annotation { "Feature Type Name" : "Feature", "Feature Type Description" : "" }
export const myFeature = defineFeature(function(context is Context, id is Id, definition is map)
    precondition{}
    {
        {
            var Q0;
            Q0=qCreatedBy(makeId("Top.planeOp"),FACE);
            var sketch = newSketch(context, id + "F0", { "sketchPlane" : qUnion([Q0])});
            skText(sketch, "E0", { "text": "DROID SANS MONO", "fontName": "DroidSansMono.ttf"});
            skText(sketch, "E1", { "text": "ALLERTA STENCIL", "fontName": "AllertaStencil-Regular.ttf"});
            skText(sketch, "E2", { "text": "ARIMO 123", "fontName": "Arimo-Bold.ttf"});
            skText(sketch, "E3", { "text": "NOTO SANS 123", "fontName": "NotoSans-Bold.ttf"});
            skText(sketch, "E4", { "text": "OPEN SANS 123", "fontName": "OpenSans-Bold.ttf"});
            skText(sketch, "E5", { "text": "ROBOTO SLAB 123", "fontName": "RobotoSlab-Bold.ttf"});
            skText(sketch, "E6", { "text": "TINOS 123", "fontName": "Tinos-Bold.ttf"});
            const initialGuessF0  = {"E0": [0, 0, 1, 0, 0.00625], "E1": [0, -0.01393, 1, 0, 0.00625], "E2": [0, -0.03032, 1, 0, 0.00625], "E3": [0, -0.04888, 1, 0, 0.00625], "E4": [0, -0.0687, 1, 0, 0.00625], "E5": [0, -0.08948, 1, 0, 0.00625], "E6": [0, -0.10994, 1, 0, 0.00625]};
            skSetInitialGuess(sketch, initialGuessF0);
            skSolve(sketch);
        }
        {
            var Q0;
            Q0 = qSketchRegion(id + "F0", true);
            extrude(context, id + "F1", {"entities" : qUnion([Q0]), "depth" : 2 * mm, "offsetDistance" : 25 * mm});
        }
        {
            var Q0;
            Q0=qCreatedBy(makeId("Top.planeOp"),FACE);
            var sketch = newSketch(context, id + "F2", { "sketchPlane" : qUnion([Q0])});
            skLineSegment(sketch, "E7.bottom", {"start": v(-1.88, -116.4) * mm, "end": v(91.82, -116.4) * mm});
            skLineSegment(sketch, "E7.top", {"start": v(-1.88, 8.51) * mm, "end": v(91.82, 8.51) * mm});
            skLineSegment(sketch, "E7.left", {"start": v(-1.88, -116.4) * mm, "end": v(-1.88, 8.51) * mm});
            skLineSegment(sketch, "E7.right", {"start": v(91.82, -116.4) * mm, "end": v(91.82, 8.51) * mm});
            skSolve(sketch);
        }
        {
            var Q0;
            Q0 = qSketchRegion(id + "F2", true);
            extrude(context, id + "F3", {"entities" : qUnion([Q0]), "operationType" : NewBodyOperationType.ADD, "oppositeDirection" : true, "depth" : 2 * mm, "offsetDistance" : 25 * mm});
        }
    });